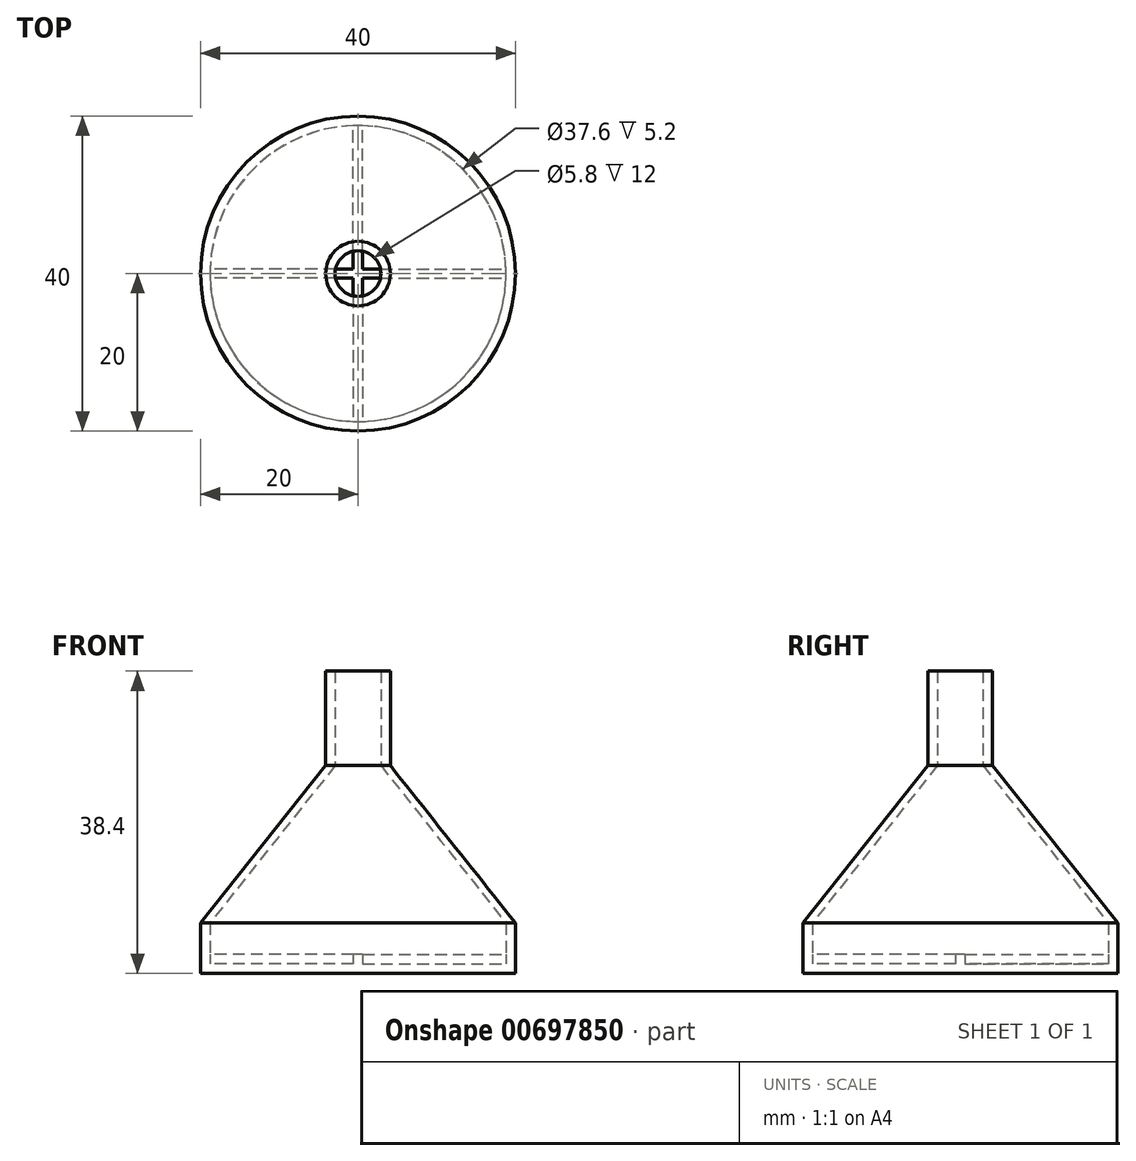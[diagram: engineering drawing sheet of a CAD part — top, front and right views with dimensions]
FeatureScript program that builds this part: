
annotation { "Feature Type Name" : "Feature", "Feature Type Description" : "" }
export const myFeature = defineFeature(function(context is Context, id is Id, definition is map)
    precondition{}
    {
        {
            assignVariable(context, id + "F0", {"name" : "Width", "anyValue" : 0.6});
        }
        {
            var Q0;
            Q0=qCreatedBy(makeId("Top.planeOp"),FACE);
            var sketch = newSketch(context, id + "F1", { "sketchPlane" : qUnion([Q0])});
            skCircle(sketch, "E0", {"center": v(0, 0) * mm, "radius": 20 * mm});
            skLineSegment(sketch, "E1", {"start": v(0, 0) * mm, "end": v(20, 0) * mm, "construction": true});
            skLineSegment(sketch, "E2", {"start": v(0, 0) * mm, "end": v(-20, 0) * mm, "construction": true});
            skLineSegment(sketch, "E3", {"start": v(0, 0) * mm, "end": v(0, 20) * mm, "construction": true});
            skLineSegment(sketch, "E4", {"start": v(0, 0) * mm, "end": v(0, -20) * mm, "construction": true});
            skLineSegment(sketch, "E5.0", {"start": v(0.6, 0.6) * mm, "end": v(0.6, 18.8) * mm});
            skLineSegment(sketch, "E6.0", {"start": v(-0.6, 0.6) * mm, "end": v(-0.6, 18.8) * mm});
            skLineSegment(sketch, "E7.0", {"start": v(-0.6, 0.6) * mm, "end": v(-18.8, 0.6) * mm});
            skLineSegment(sketch, "E8.0", {"start": v(-0.6, -0.6) * mm, "end": v(-18.8, -0.6) * mm});
            skLineSegment(sketch, "E9.0", {"start": v(0.6, -0.6) * mm, "end": v(18.8, -0.6) * mm});
            skLineSegment(sketch, "E10.0", {"start": v(0.6, 0.6) * mm, "end": v(18.8, 0.6) * mm});
            skLineSegment(sketch, "E11.0", {"start": v(-0.6, -0.6) * mm, "end": v(-0.6, -18.8) * mm});
            skLineSegment(sketch, "E12.0", {"start": v(0.6, -0.6) * mm, "end": v(0.6, -18.8) * mm});
            skArc(sketch, "E13.0", {"start": v(-18.8, -0.6) * mm, "mid": v(-13.3, -13.3) * mm, "end": v(-0.6, -18.8) * mm});
            skArc(sketch, "E14.trimOffspring", {"start": v(18.8, 0.6) * mm, "mid": v(13.3, 13.3) * mm, "end": v(0.6, 18.8) * mm});
            skArc(sketch, "E15.trimOffspring", {"start": v(0.6, -18.8) * mm, "mid": v(13.3, -13.3) * mm, "end": v(18.8, -0.6) * mm});
            skArc(sketch, "E16.trimOffspring", {"start": v(-0.6, 18.8) * mm, "mid": v(-13.3, 13.3) * mm, "end": v(-18.8, 0.6) * mm});
            skSolve(sketch);
        }
        {
            var Q0;
            Q0=makeQuery(id+"F1.imprint","IMPRINT",FACE,{"disambiguationData":[TD([[makeQuery(id+"F1.imprint","IMPRINT",EDGE,{"derivedFrom":sQuery(id+"F1.wireOp",EDGE,"E0")}),1.0]])]});
            extrude(context, id + "F2", {"entities" : qUnion([Q0]), "depth" : (getVariable(context, 'Width') * 2) * mm, "offsetDistance" : 25 * mm});
        }
        {
            var Q0;
            Q0=qCreatedBy(makeId("Top.planeOp"),FACE);
            var sketch = newSketch(context, id + "F3", { "sketchPlane" : qUnion([Q0])});
            skCircle(sketch, "E17.0", {"center": v(0, 0) * mm, "radius": 20 * mm});
            skSolve(sketch);
        }
        {
            var Q0;
            Q0=makeQuery(id+"F3.imprint","IMPRINT",FACE,{"disambiguationData":[TD([[makeQuery(id+"F3.imprint","IMPRINT",EDGE,{"derivedFrom":sQuery(id+"F3.wireOp",EDGE,"E17.0")}),1.0]])]});
            extrude(context, id + "F4", {"entities" : qUnion([Q0]), "operationType" : NewBodyOperationType.ADD, "oppositeDirection" : true, "depth" : (getVariable(context, 'Width') * 2) * mm, "offsetDistance" : 25 * mm});
        }
        {
            var Q0;
            Q0=makeQuery(id+"F2.opExtrude","CAP_FACE",FACE,{"disambiguationData":[OSD([sQuery(id+"F1.wireOp",EDGE,"E0"),sQuery(id+"F1.wireOp",EDGE,"E5.0"),sQuery(id+"F1.wireOp",EDGE,"E6.0"),sQuery(id+"F1.wireOp",EDGE,"E7.0"),sQuery(id+"F1.wireOp",EDGE,"E8.0"),sQuery(id+"F1.wireOp",EDGE,"E9.0"),sQuery(id+"F1.wireOp",EDGE,"E10.0"),sQuery(id+"F1.wireOp",EDGE,"E11.0"),sQuery(id+"F1.wireOp",EDGE,"E12.0"),sQuery(id+"F1.wireOp",EDGE,"E13.0"),sQuery(id+"F1.wireOp",EDGE,"E14.trimOffspring"),sQuery(id+"F1.wireOp",EDGE,"E15.trimOffspring"),sQuery(id+"F1.wireOp",EDGE,"E16.trimOffspring")])],"isStart":false});
            cPlane(context, id + "F5", {"entities" : qUnion([Q0]), "cplaneType" : CPlaneType.OFFSET, "offset" : 0 * mm, "width" : 150 * mm, "height" : 150 * mm});
        }
        {
            var Q0;
            Q0=qCreatedBy(id+"F5.planeOp",FACE);
            var sketch = newSketch(context, id + "F6", { "sketchPlane" : qUnion([Q0])});
            skCircle(sketch, "E18.0", {"center": v(0, 0) * mm, "radius": 20 * mm});
            skCircle(sketch, "E19.0", {"center": v(0, 0) * mm, "radius": 18.8 * mm});
            skSolve(sketch);
        }
        {
            var Q0;
            Q0=makeQuery(id+"F6.imprint","IMPRINT",FACE,{"disambiguationData":[TD([[makeQuery(id+"F6.imprint","IMPRINT",EDGE,{"derivedFrom":sQuery(id+"F6.wireOp",EDGE,"E18.0")}),1.0]])]});
            extrude(context, id + "F7", {"entities" : qUnion([Q0]), "operationType" : NewBodyOperationType.ADD, "depth" : 4 * mm, "offsetDistance" : 25 * mm});
        }
        {
            var Q0;
            Q0=makeQuery(id+"F7.opExtrude","CAP_FACE",FACE,{"disambiguationData":[OSD([sQuery(id+"F6.wireOp",EDGE,"E18.0"),sQuery(id+"F6.wireOp",EDGE,"E19.0")])],"isStart":false});
            cPlane(context, id + "F8", {"entities" : qUnion([Q0]), "cplaneType" : CPlaneType.OFFSET, "offset" : 0 * mm, "width" : 150 * mm, "height" : 150 * mm});
        }
        {
            var Q0;
            Q0=qCreatedBy(id+"F8.planeOp",FACE);
            var sketch = newSketch(context, id + "F9", { "sketchPlane" : qUnion([Q0])});
            skCircle(sketch, "E20.0", {"center": v(0, 0) * mm, "radius": 20 * mm});
            skSolve(sketch);
        }
        {
            var Q0;
            Q0=qCreatedBy(id+"F8.planeOp",FACE);
            cPlane(context, id + "F10", {"entities" : qUnion([Q0]), "cplaneType" : CPlaneType.OFFSET, "offset" : 20 * mm, "width" : 150 * mm, "height" : 150 * mm});
        }
        {
            var Q0;
            Q0=qCreatedBy(id+"F10.planeOp",FACE);
            var sketch = newSketch(context, id + "F11", { "sketchPlane" : qUnion([Q0])});
            skCircle(sketch, "E21", {"center": v(0, 0) * mm, "radius": 4.1 * mm});
            skSolve(sketch);
        }
        {
            var Q1;
            Q1=makeQuery(id+"F9.imprint","IMPRINT",FACE,{"disambiguationData":[TD([[makeQuery(id+"F9.imprint","IMPRINT",EDGE,{"derivedFrom":sQuery(id+"F9.wireOp",EDGE,"E20.0")}),1.0]])]});
            var Q2;
            Q2=makeQuery(id+"F11.imprint","IMPRINT",FACE,{"disambiguationData":[TD([[makeQuery(id+"F11.imprint","IMPRINT",EDGE,{"derivedFrom":sQuery(id+"F11.wireOp",EDGE,"E21")}),1.0]])]});
            loft(context, id + "F12", {"operationType" : NewBodyOperationType.ADD, "sheetProfilesArray" : [{ "sheetProfileEntities" : qUnion([Q1]) }, { "sheetProfileEntities" : qUnion([Q2]) }]});
        }
        {
            var Q0;
            Q0=makeQuery(id+"F12.opLoft","CAP_FACE",FACE,{"disambiguationData":[OSD([makeQuery(id+"F11.imprint","IMPRINT",FACE,{"disambiguationData":[TD([[makeQuery(id+"F11.imprint","IMPRINT",EDGE,{"derivedFrom":sQuery(id+"F11.wireOp",EDGE,"E21")}),1.0]])]})])],"isStart":true});
            extrude(context, id + "F13", {"entities" : qUnion([Q0]), "operationType" : NewBodyOperationType.ADD, "depth" : 12 * mm, "offsetDistance" : 25 * mm});
        }
        {
            var Q0;
            Q0=qCreatedBy(id+"F8.planeOp",FACE);
            var sketch = newSketch(context, id + "F14", { "sketchPlane" : qUnion([Q0])});
            skCircle(sketch, "E22.0", {"center": v(0, 0) * mm, "radius": 20 * mm, "construction": true});
            skCircle(sketch, "E23.0", {"center": v(0, 0) * mm, "radius": 18.8 * mm});
            skSolve(sketch);
        }
        {
            var Q0;
            Q0=qCreatedBy(id+"F10.planeOp",FACE);
            var sketch = newSketch(context, id + "F15", { "sketchPlane" : qUnion([Q0])});
            skCircle(sketch, "E24.0", {"center": v(0, 0) * mm, "radius": 4.1 * mm, "construction": true});
            skCircle(sketch, "E25.0", {"center": v(0, 0) * mm, "radius": 2.9 * mm});
            skSolve(sketch);
        }
        {
            var Q0;
            Q0=qSketchRegion(id+"F15",true);
            extrude(context, id + "F16", {"entities" : qUnion([Q0]), "operationType" : NewBodyOperationType.REMOVE, "depth" : 25 * mm, "offsetDistance" : 25 * mm});
        }
        {
            var Q1;
            Q1=qSketchRegion(id+"F14",true);
            var Q2;
            Q2=qSketchRegion(id+"F15",true);
            loft(context, id + "F17", {"operationType" : NewBodyOperationType.REMOVE, "sheetProfilesArray" : [{ "sheetProfileEntities" : qUnion([Q1]) }, { "sheetProfileEntities" : qUnion([Q2]) }]});
        }
    });
